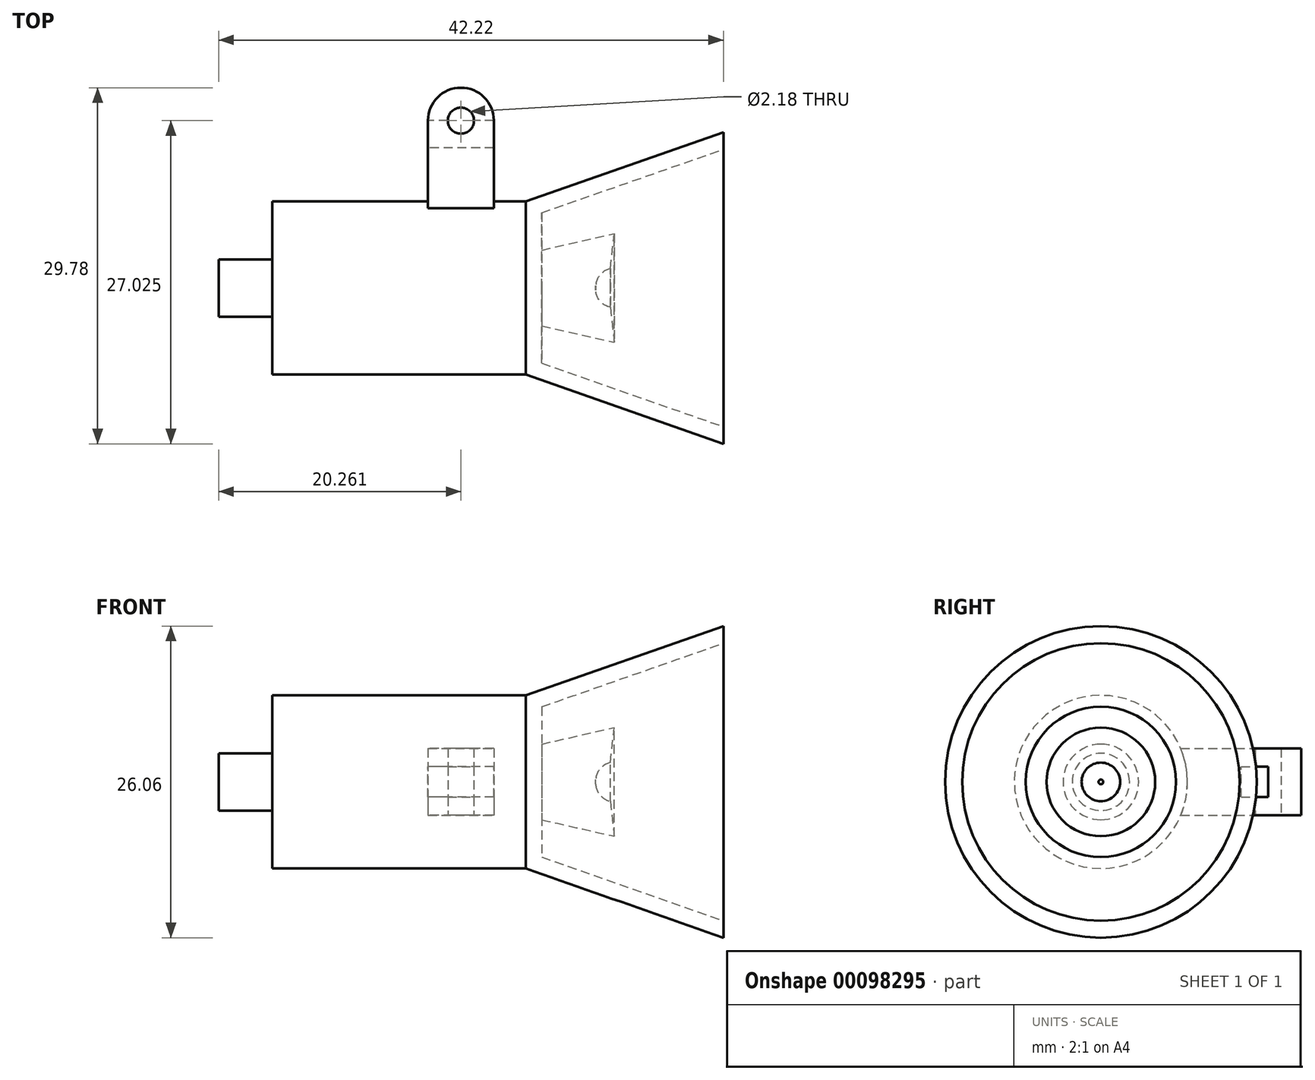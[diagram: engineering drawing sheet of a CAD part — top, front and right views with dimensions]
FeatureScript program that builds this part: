
annotation { "Feature Type Name" : "Feature", "Feature Type Description" : "" }
export const myFeature = defineFeature(function(context is Context, id is Id, definition is map)
    precondition{}
    {
        {
            var Q0;
            Q0=qCreatedBy(makeId("Front.planeOp"),FACE);
            var sketch = newSketch(context, id + "F0", { "sketchPlane" : qUnion([Q0])});
            skLineSegment(sketch, "E0", {"start": v(-21.18, 0) * mm, "end": v(-21.18, 7.24) * mm});
            skLineSegment(sketch, "E1", {"start": v(-21.18, 7.24) * mm, "end": v(0, 7.24) * mm});
            skLineSegment(sketch, "E2", {"start": v(0, 7.24) * mm, "end": v(0, 7.24) * mm});
            skLineSegment(sketch, "E3", {"start": v(0, 7.24) * mm, "end": v(0, 0) * mm});
            skLineSegment(sketch, "E4", {"start": v(0, 0) * mm, "end": v(-21.18, 0) * mm});
            skLineSegment(sketch, "E5", {"start": v(0, 7.24) * mm, "end": v(16.54, 13.03) * mm});
            skLineSegment(sketch, "E6", {"start": v(16.54, 13.03) * mm, "end": v(16.54, 0) * mm});
            skLineSegment(sketch, "E7", {"start": v(16.54, 0) * mm, "end": v(0, 0) * mm});
            skSolve(sketch);
        }
        {
            var Q0;
            Q0=makeQuery(id+"F0.imprint","IMPRINT",FACE,{"disambiguationData":[TD([[makeQuery(id+"F0.imprint","IMPRINT",EDGE,{"derivedFrom":sQuery(id+"F0.wireOp",EDGE,"E3")}),1.0]])]});
            var Q1;
            Q1=sQuery(id+"F0.wireOp",EDGE,"E4");
            revolve(context, id + "F1", {"entities" : qUnion([Q0]), "axis" : qUnion([Q1]), "revolveType" : RevolveType.FULL});
        }
        {
            var Q0;
            Q0=makeQuery(id+"F1.opRevolve","SWEPT_FACE",FACE,{"disambiguationData":[OSD([sQuery(id+"F0.wireOp",EDGE,"E6")])]});
            shell(context, id + "F2", {"entities" : qUnion([Q0]), "thickness" : 1.35 * mm});
        }
        {
            var Q0;
            Q0=makeQuery(id+"F0.imprint","IMPRINT",FACE,{"disambiguationData":[TD([[makeQuery(id+"F0.imprint","IMPRINT",EDGE,{"derivedFrom":sQuery(id+"F0.wireOp",EDGE,"E0")}),-1.0]])]});
            var Q1;
            Q1=sQuery(id+"F0.wireOp",EDGE,"E4");
            revolve(context, id + "F3", {"operationType" : NewBodyOperationType.ADD, "entities" : qUnion([Q0]), "axis" : qUnion([Q1]), "revolveType" : RevolveType.FULL});
        }
        {
            var Q0;
            Q0=makeQuery(id+"F3.opRevolve","SWEPT_FACE",FACE,{"disambiguationData":[OSD([sQuery(id+"F0.wireOp",EDGE,"E0")])]});
            var sketch = newSketch(context, id + "F4", { "sketchPlane" : qUnion([Q0])});
            skCircle(sketch, "E8", {"center": v(0, 0) * mm, "radius": 2.4 * mm});
            skSolve(sketch);
        }
        {
            var Q0;
            Q0 = qSketchRegion(id + "F4", true);
            extrude(context, id + "F5", {"entities" : qUnion([Q0]), "operationType" : NewBodyOperationType.ADD, "depth" : 4.5 * mm});
        }
        {
            var Q0;
            Q0=qCreatedBy(makeId("Top.planeOp"),FACE);
            var sketch = newSketch(context, id + "F6", { "sketchPlane" : qUnion([Q0])});
            skLineSegment(sketch, "E9.bottom", {"start": v(-8.17, 4.55) * mm, "end": v(-2.66, 4.55) * mm});
            skLineSegment(sketch, "E9.top", {"start": v(-8.17, 14) * mm, "end": v(-2.66, 14) * mm});
            skLineSegment(sketch, "E9.left", {"start": v(-8.17, 4.55) * mm, "end": v(-8.17, 14) * mm});
            skLineSegment(sketch, "E9.right", {"start": v(-2.66, 4.55) * mm, "end": v(-2.66, 14) * mm});
            skPoint(sketch, "E10.centerSnap0", {"position": v(-5.42, 14) * mm});
            skLineSegment(sketch, "E11", {"start": v(-21.18, 7.24) * mm, "end": v(0, 7.24) * mm, "construction": true});
            skCircle(sketch, "E12", {"center": v(-5.42, 14) * mm, "radius": 1.1 * mm});
            skCircle(sketch, "E13", {"center": v(-5.42, 14) * mm, "radius": 2.76 * mm});
            skSolve(sketch);
        }
        {
            var Q0;
            Q0 = qSketchRegion(id + "F6", true);
            extrude(context, id + "F7", {"entities" : qUnion([Q0]), "operationType" : NewBodyOperationType.ADD, "endBound" : BoundingType.SYMMETRIC, "depth" : 5.6 * mm});
        }
        {
            var Q0;
            Q0=makeQuery(id+"F7.opExtrude","SWEPT_FACE",FACE,{"disambiguationData":[OSD([sQuery(id+"F6.wireOp",EDGE,"E9.left")])]});
            var sketch = newSketch(context, id + "F8", { "sketchPlane" : qUnion([Q0])});
            skLineSegment(sketch, "E14.bottom", {"start": v(-11.72, -1.27) * mm, "end": v(-16.75, -1.27) * mm});
            skLineSegment(sketch, "E14.top", {"start": v(-11.72, 1.27) * mm, "end": v(-16.75, 1.27) * mm});
            skLineSegment(sketch, "E14.left", {"start": v(-11.72, -1.27) * mm, "end": v(-11.72, 1.27) * mm});
            skLineSegment(sketch, "E14.right", {"start": v(-16.75, -1.27) * mm, "end": v(-16.75, 1.27) * mm});
            skLineSegment(sketch, "E15", {"start": v(-16.75, -2.8) * mm, "end": v(-16.75, 2.8) * mm});
            skSolve(sketch);
        }
        {
            var Q0;
            {var subQ0=sQuery(id+"F8.wireOp",EDGE,"E14.left");Q0=makeQuery(id+"F8.imprint","IMPRINT",FACE,{"disambiguationData":[TD([[makeQuery(id+"F8.imprint","IMPRINT",EDGE,{"derivedFrom":subQ0}),1.0]])]});}
            var Q1;
            {var subQ0=sQuery(id+"F8.wireOp",EDGE,"E15");var subQ1=sQuery(id+"F8.wireOp",EDGE,"E14.bottom");var subQ2=makeQuery(id+"F8.imprint","INTERSECT",VERTEX,{"derivedFrom":[subQ1,subQ0]});Q1=makeQuery(id+"F8.imprint","IMPRINT",FACE,{"disambiguationData":[TD([[makeQuery(id+"F8.imprint","IMPRINT",EDGE,{"disambiguationData":[TD([[subQ2,-1.0]])],"derivedFrom":subQ0}),-1.0]])]});}
            var Q2;
            Q2=makeQuery(id+"F7.opExtrude","SWEPT_FACE",FACE,{"disambiguationData":[OSD([sQuery(id+"F6.wireOp",EDGE,"E9.right")])]});
            extrude(context, id + "F9", {"entities" : qUnion([Q0, Q1]), "operationType" : NewBodyOperationType.REMOVE, "oppositeDirection" : true, "endBoundEntityFace" : qUnion([Q2]), "depth" : 10.16 * mm});
        }
        {
            var Q0;
            Q0=qCreatedBy(makeId("Front.planeOp"),FACE);
            var sketch = newSketch(context, id + "F10", { "sketchPlane" : qUnion([Q0])});
            skLineSegment(sketch, "E16", {"start": v(0, 2.86) * mm, "end": v(7.4, 4.54) * mm});
            skLineSegment(sketch, "E17", {"start": v(7.4, 4.54) * mm, "end": v(7.08, 1.61) * mm});
            skArc(sketch, "E18", {"start": v(8.95, 0) * mm, "mid": v(8.42, 1.27) * mm, "end": v(7.08, 1.61) * mm});
            skLineSegment(sketch, "E19", {"start": v(0, 2.86) * mm, "end": v(0, 0) * mm});
            skLineSegment(sketch, "E20", {"start": v(0, 0) * mm, "end": v(8.95, 0) * mm});
            skSolve(sketch);
        }
        {
            var Q0;
            Q0 = qSketchRegion(id + "F10", true);
            var Q1;
            Q1=sQuery(id+"F0.wireOp",EDGE,"E7");
            revolve(context, id + "F11", {"operationType" : NewBodyOperationType.ADD, "entities" : qUnion([Q0]), "axis" : qUnion([Q1]), "revolveType" : RevolveType.FULL});
        }
    });
